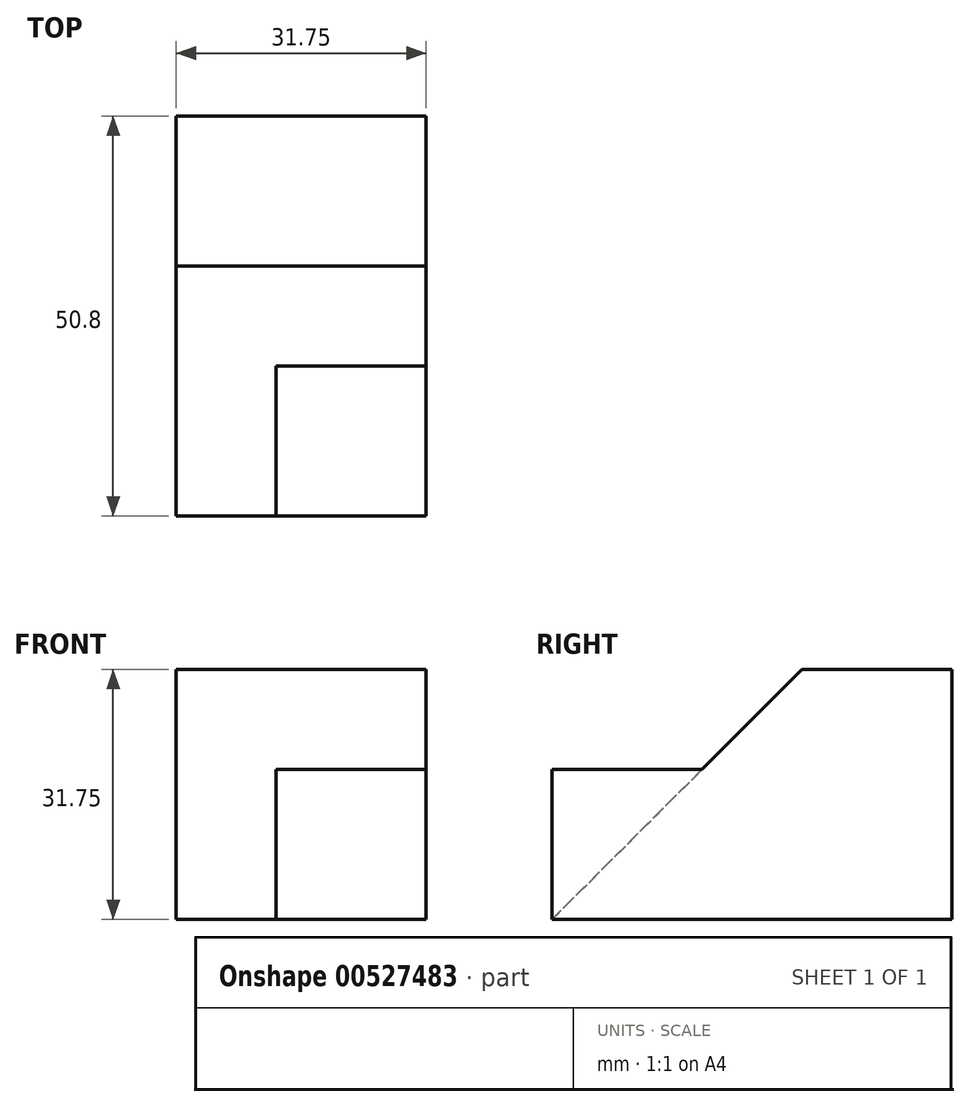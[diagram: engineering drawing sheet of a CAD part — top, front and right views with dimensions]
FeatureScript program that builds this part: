
annotation { "Feature Type Name" : "Feature", "Feature Type Description" : "" }
export const myFeature = defineFeature(function(context is Context, id is Id, definition is map)
    precondition{}
    {
        {
            var Q0;
            Q0=qCreatedBy(makeId("Right.planeOp"),FACE);
            var sketch = newSketch(context, id + "F0", { "sketchPlane" : qUnion([Q0])});
            skLineSegment(sketch, "E0", {"start": v(0, 0) * mm, "end": v(50.8, 0) * mm});
            skLineSegment(sketch, "E1", {"start": v(0, 0) * mm, "end": v(0, 31.75) * mm});
            skLineSegment(sketch, "E2", {"start": v(0, 31.75) * mm, "end": v(50.8, 31.75) * mm});
            skLineSegment(sketch, "E3", {"start": v(50.8, 31.75) * mm, "end": v(50.8, 0) * mm});
            skSolve(sketch);
        }
        {
            var Q0;
            Q0 = qSketchRegion(id + "F0", true);
            extrude(context, id + "F1", {"entities" : qUnion([Q0]), "oppositeDirection" : true, "depth" : 31.75 * mm, "offsetDistance" : 25.4 * mm});
        }
        {
            var Q0;
            Q0=makeQuery(id+"F1.opExtrude","CAP_FACE",FACE,{"disambiguationData":[OSD([sQuery(id+"F0.wireOp",EDGE,"E0"),sQuery(id+"F0.wireOp",EDGE,"E1"),sQuery(id+"F0.wireOp",EDGE,"E2"),sQuery(id+"F0.wireOp",EDGE,"E3")])],"isStart":false});
            var sketch = newSketch(context, id + "F2", { "sketchPlane" : qUnion([Q0])});
            skLineSegment(sketch, "E4", {"start": v(-31.75, 31.75) * mm, "end": v(0, 0) * mm});
            skSolve(sketch);
        }
        {
            var Q0;
            {var subQ0=sQuery(id+"F2.wireOp",EDGE,"E4");Q0=makeQuery(id+"F2.imprint","IMPRINT",FACE,{"disambiguationData":[TD([[makeQuery(id+"F2.imprint","IMPRINT",EDGE,{"derivedFrom":subQ0}),1.0]])]});}
            extrude(context, id + "F3", {"entities" : qUnion([Q0]), "operationType" : NewBodyOperationType.REMOVE, "oppositeDirection" : true, "depth" : 12.7 * mm, "offsetDistance" : 25.4 * mm});
        }
        {
            var Q0;
            Q0=makeQuery(id+"F3.boolean.opBoolean","COPY",FACE,{"derivedFrom":makeQuery(id+"F3.opExtrude","CAP_FACE",FACE,{"disambiguationData":[OSD([sQuery(id+"F0.wireOp",EDGE,"E1"),sQuery(id+"F0.wireOp",EDGE,"E2"),sQuery(id+"F2.wireOp",EDGE,"E4")])],"isStart":false})});
            var sketch = newSketch(context, id + "F4", { "sketchPlane" : qUnion([Q0])});
            skLineSegment(sketch, "E5", {"start": v(-19.05, 19.05) * mm, "end": v(0, 19.05) * mm});
            skSolve(sketch);
        }
        {
            var Q0;
            {var subQ0=sQuery(id+"F4.wireOp",EDGE,"E5");Q0=makeQuery(id+"F4.imprint","IMPRINT",FACE,{"disambiguationData":[TD([[makeQuery(id+"F4.imprint","IMPRINT",EDGE,{"derivedFrom":subQ0}),1.0]])]});}
            extrude(context, id + "F5", {"entities" : qUnion([Q0]), "operationType" : NewBodyOperationType.REMOVE, "oppositeDirection" : true, "depth" : 19.05 * mm, "offsetDistance" : 25.4 * mm});
        }
    });
